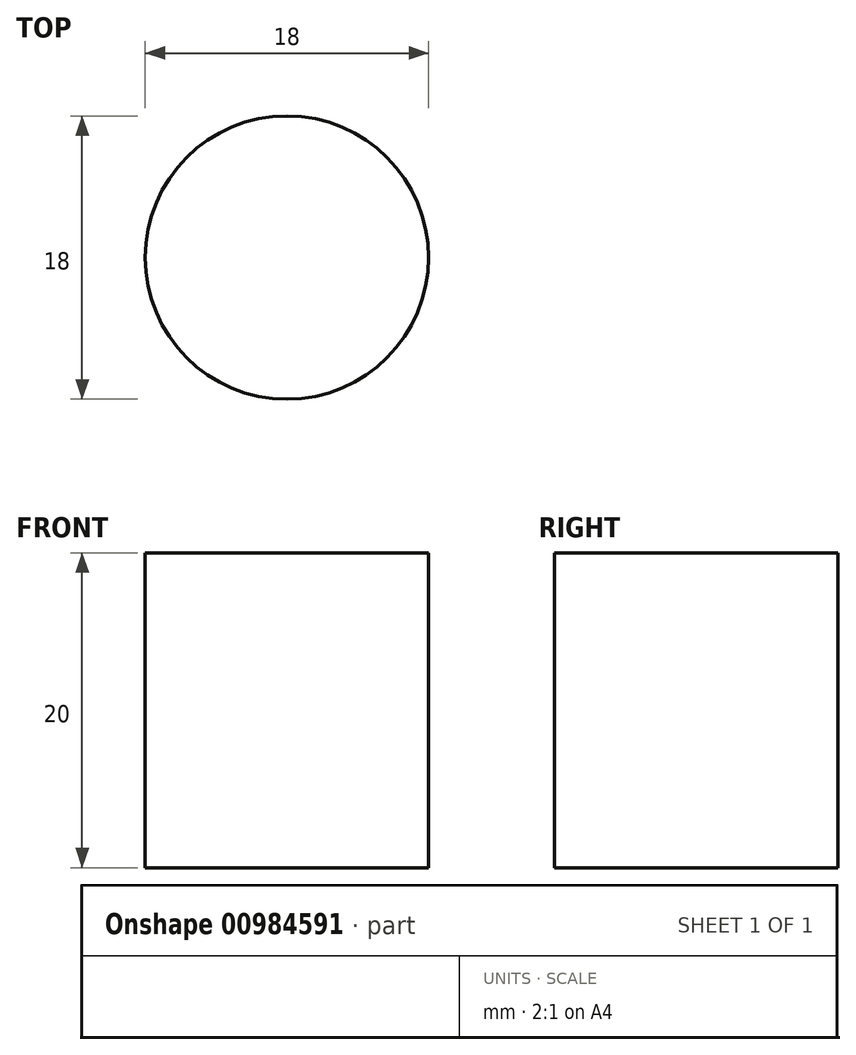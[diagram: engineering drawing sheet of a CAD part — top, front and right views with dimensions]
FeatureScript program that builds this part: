
annotation { "Feature Type Name" : "Feature", "Feature Type Description" : "" }
export const myFeature = defineFeature(function(context is Context, id is Id, definition is map)
    precondition{}
    {
        {
            var Q0;
            Q0=qCreatedBy(makeId("Top.planeOp"),FACE);
            var sketch = newSketch(context, id + "F0", { "sketchPlane" : qUnion([Q0])});
            skCircle(sketch, "E0", {"center": v(0, 0) * mm, "radius": 9 * mm});
            skLineSegment(sketch, "E1.bottom", {"start": v(2, 2) * mm, "end": v(-2, 2) * mm});
            skLineSegment(sketch, "E1.top", {"start": v(2, -2) * mm, "end": v(-2, -2) * mm});
            skLineSegment(sketch, "E1.left", {"start": v(2, 2) * mm, "end": v(2, -2) * mm});
            skLineSegment(sketch, "E1.right", {"start": v(-2, 2) * mm, "end": v(-2, -2) * mm});
            skSolve(sketch);
        }
        {
            var Q0;
            Q0=makeQuery(id+"F0.imprint","IMPRINT",FACE,{"disambiguationData":[TD([[makeQuery(id+"F0.imprint","IMPRINT",EDGE,{"derivedFrom":sQuery(id+"F0.wireOp",EDGE,"E1.bottom")}),1.0]])]});
            var Q1;
            Q1=makeQuery(id+"F0.imprint","IMPRINT",FACE,{"disambiguationData":[TD([[makeQuery(id+"F0.imprint","IMPRINT",EDGE,{"derivedFrom":sQuery(id+"F0.wireOp",EDGE,"E0")}),1.0]])]});
            extrude(context, id + "F1", {"entities" : qUnion([Q0, Q1]), "depth" : 20 * mm, "offsetDistance" : 25 * mm});
        }
    });
